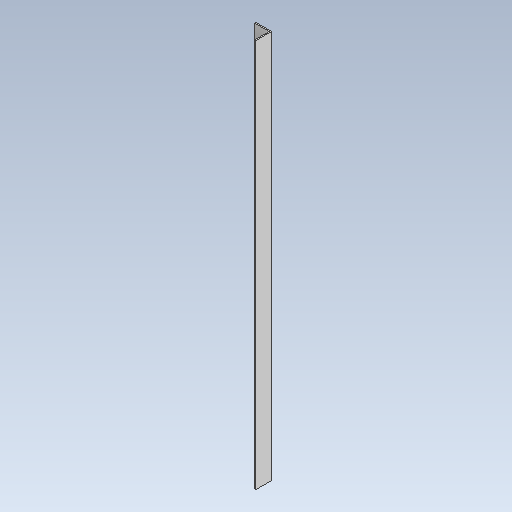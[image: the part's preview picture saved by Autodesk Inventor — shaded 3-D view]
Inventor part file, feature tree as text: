
AUTODESK INVENTOR PART (.ipt)
format: ipt  version: 2020.1 (Build 241239000, 239)  size: 102,912 bytes
history: native  units: mm
features: other x1, extrude x1, sketch x1
ambient origin geometry x8: Origin, YZ Plane, XZ Plane, XY Plane, X Axis, Y Axis, Z Axis, Center Point
bodies: Body1 (feature_tree)
feature tree (3):
  other  "Твердое тело1"
  extrude  "Выдавливание1"  Depth=3.0mm
  sketch  "Эскиз1"
